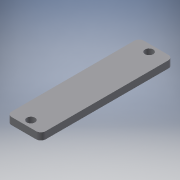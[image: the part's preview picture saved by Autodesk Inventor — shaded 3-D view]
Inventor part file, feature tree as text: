
AUTODESK INVENTOR PART (.ipt)
format: ipt  version: 2018 (Build 220112000, 112)  size: 132,608 bytes
history: native  units: mm
features: reference x4, other x3, extrude x2, sketch x2, projected_geometry x1
ambient origin geometry x8: Origin, YZ Plane, XZ Plane, XY Plane, X Axis, Y Axis, Z Axis, Center Point
bodies: Solid1 (feature_tree)
feature tree (12):
  extrude  "Extrusion1"  Depth=3.0mm TaperAngle=0.0deg
  extrude  "Extrusion2"  Depth=3.0mm
  sketch  "Sketch1"  dims[d0=2.0mm d1=3.0mm d2=0.0mm]
  reference  "Reference1"
  reference  "Reference2"
  sketch  "Sketch2"  dims[d3=3.0mm d4=3.5mm d5=3.0mm d6=3.5mm d7=3.0mm d8=0.0mm]
  reference  "Reference3"
  reference  "Reference4"
  projected_geometry  "Projected Loop1"
  other  "<userpath>\OneDrive\Documents\Inventor\TSA\2018\Animatronics\Tortoise\TurtleAssembly2.iam"
  other  "TurtleAssembly2.iam"
  other  "steer_servo_mount:1"
